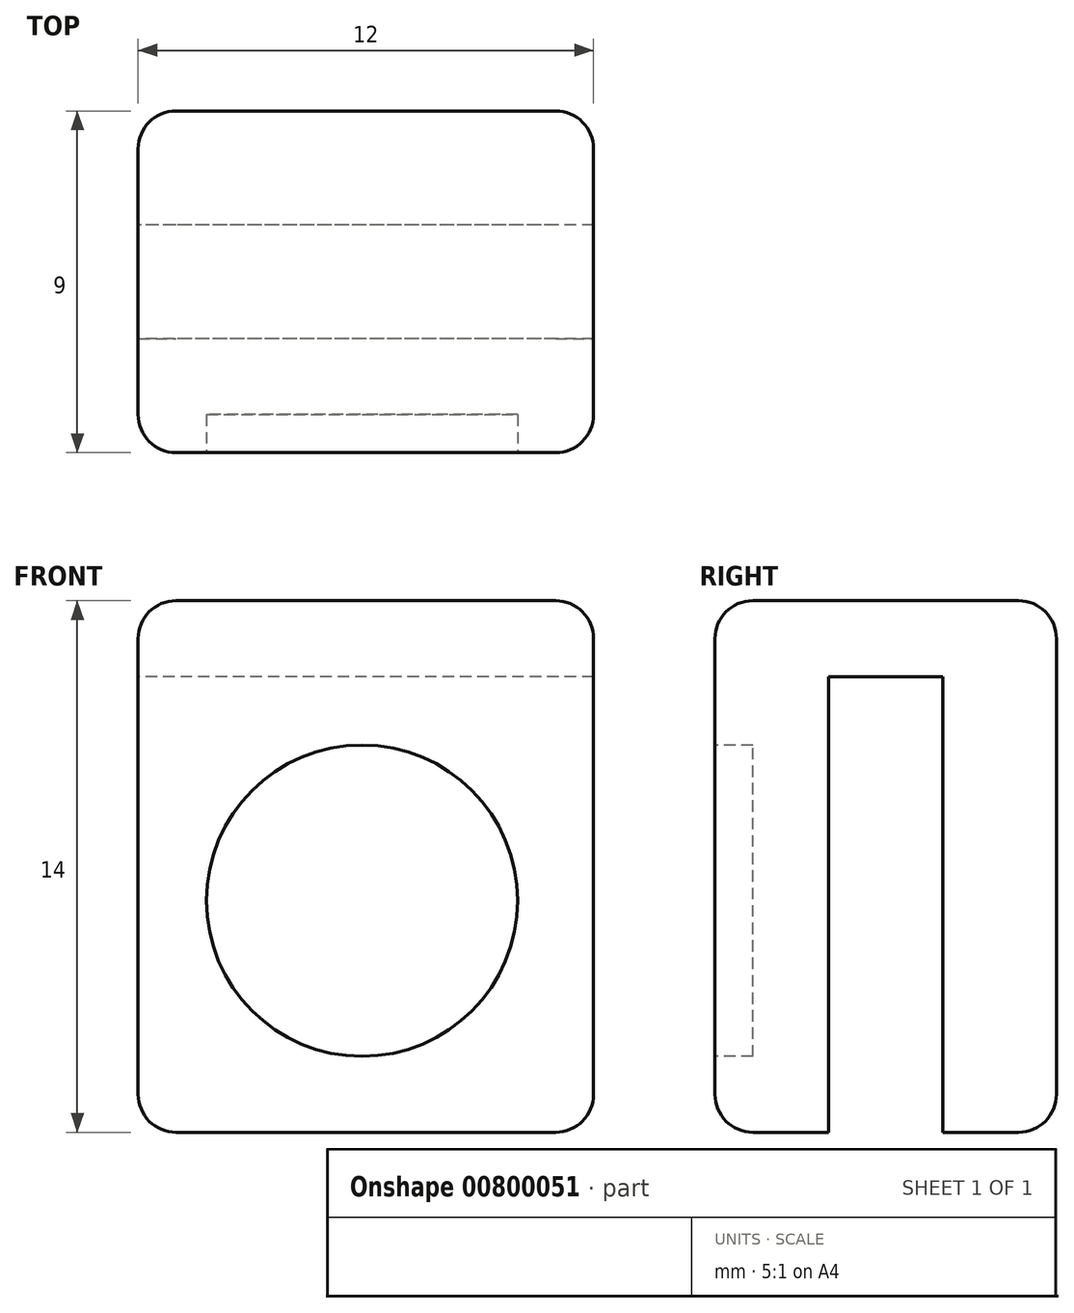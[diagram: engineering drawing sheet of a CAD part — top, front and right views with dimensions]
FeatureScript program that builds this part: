
annotation { "Feature Type Name" : "Feature", "Feature Type Description" : "" }
export const myFeature = defineFeature(function(context is Context, id is Id, definition is map)
    precondition{}
    {
        {
            var Q0;
            Q0=qCreatedBy(makeId("Front.planeOp"),FACE);
            var sketch = newSketch(context, id + "F0", { "sketchPlane" : qUnion([Q0])});
            skLineSegment(sketch, "E0", {"start": v(0, 0) * mm, "end": v(0, 14) * mm});
            skLineSegment(sketch, "E1", {"start": v(0, 14) * mm, "end": v(12, 14) * mm});
            skLineSegment(sketch, "E2", {"start": v(12, 14) * mm, "end": v(12, 0) * mm});
            skLineSegment(sketch, "E3", {"start": v(12, 0) * mm, "end": v(0, 0) * mm});
            skSolve(sketch);
        }
        {
            var Q0;
            Q0=makeQuery(id+"F0.imprint","IMPRINT",FACE,{"disambiguationData":[TD([[makeQuery(id+"F0.imprint","IMPRINT",EDGE,{"derivedFrom":sQuery(id+"F0.wireOp",EDGE,"E0")}),-1.0]])]});
            extrude(context, id + "F1", {"entities" : qUnion([Q0]), "depth" : 3 * mm, "offsetDistance" : 25 * mm});
        }
        {
            var Q0;
            Q0=makeQuery(id+"F1.opExtrude","CAP_FACE",FACE,{"disambiguationData":[OSD([sQuery(id+"F0.wireOp",EDGE,"E0"),sQuery(id+"F0.wireOp",EDGE,"E1"),sQuery(id+"F0.wireOp",EDGE,"E2"),sQuery(id+"F0.wireOp",EDGE,"E3")])],"isStart":false});
            var sketch = newSketch(context, id + "F2", { "sketchPlane" : qUnion([Q0])});
            skCircle(sketch, "E4", {"center": v(5.9, 6.1) * mm, "radius": 4.1 * mm});
            skSolve(sketch);
        }
        {
            var Q0;
            Q0=makeQuery(id+"F2.imprint","IMPRINT",FACE,{"disambiguationData":[TD([[makeQuery(id+"F2.imprint","IMPRINT",EDGE,{"derivedFrom":sQuery(id+"F2.wireOp",EDGE,"E4")}),1.0]])]});
            extrude(context, id + "F3", {"entities" : qUnion([Q0]), "operationType" : NewBodyOperationType.REMOVE, "oppositeDirection" : true, "depth" : 1 * mm, "offsetDistance" : 25 * mm});
        }
        {
            var Q0;
            Q0=makeQuery(id+"F1.opExtrude","CAP_FACE",FACE,{"disambiguationData":[OSD([sQuery(id+"F0.wireOp",EDGE,"E0"),sQuery(id+"F0.wireOp",EDGE,"E1"),sQuery(id+"F0.wireOp",EDGE,"E2"),sQuery(id+"F0.wireOp",EDGE,"E3")])],"isStart":true});
            var sketch = newSketch(context, id + "F4", { "sketchPlane" : qUnion([Q0])});
            skLineSegment(sketch, "E5.bottom", {"start": v(-12, 14) * mm, "end": v(0, 14) * mm});
            skLineSegment(sketch, "E5.top", {"start": v(-12, 12) * mm, "end": v(0, 12) * mm});
            skLineSegment(sketch, "E5.left", {"start": v(-12, 14) * mm, "end": v(-12, 12) * mm});
            skLineSegment(sketch, "E5.right", {"start": v(0, 14) * mm, "end": v(0, 12) * mm});
            skSolve(sketch);
        }
        {
            var Q0;
            Q0=makeQuery(id+"F4.imprint","IMPRINT",FACE,{"disambiguationData":[TD([[makeQuery(id+"F4.imprint","IMPRINT",EDGE,{"derivedFrom":sQuery(id+"F4.wireOp",EDGE,"E5.bottom")}),1.0]])]});
            extrude(context, id + "F5", {"entities" : qUnion([Q0]), "operationType" : NewBodyOperationType.ADD, "depth" : 3 * mm, "offsetDistance" : 25 * mm});
        }
        {
            var Q0;
            Q0=makeQuery(id+"F5.opExtrude","CAP_FACE",FACE,{"disambiguationData":[OSD([sQuery(id+"F4.wireOp",EDGE,"E5.bottom"),sQuery(id+"F4.wireOp",EDGE,"E5.top"),sQuery(id+"F4.wireOp",EDGE,"E5.left"),sQuery(id+"F4.wireOp",EDGE,"E5.right")])],"isStart":false});
            var sketch = newSketch(context, id + "F6", { "sketchPlane" : qUnion([Q0])});
            skLineSegment(sketch, "E6.bottom", {"start": v(-12, 14) * mm, "end": v(0, 14) * mm});
            skLineSegment(sketch, "E6.top", {"start": v(-12, 0) * mm, "end": v(0, 0) * mm});
            skLineSegment(sketch, "E6.left", {"start": v(-12, 14) * mm, "end": v(-12, 0) * mm});
            skLineSegment(sketch, "E6.right", {"start": v(0, 14) * mm, "end": v(0, 0) * mm});
            skSolve(sketch);
        }
        {
            var Q0;
            {var subQ0=sQuery(id+"F6.wireOp",EDGE,"E6.bottom");Q0=makeQuery(id+"F6.imprint","IMPRINT",FACE,{"disambiguationData":[TD([[makeQuery(id+"F6.imprint","IMPRINT",EDGE,{"derivedFrom":subQ0}),1.0]])]});}
            var Q1;
            {var subQ0=sQuery(id+"F6.wireOp",EDGE,"E6.top");Q1=makeQuery(id+"F6.imprint","IMPRINT",FACE,{"disambiguationData":[TD([[makeQuery(id+"F6.imprint","IMPRINT",EDGE,{"derivedFrom":subQ0}),1.0]])]});}
            extrude(context, id + "F7", {"entities" : qUnion([Q0, Q1]), "operationType" : NewBodyOperationType.ADD, "depth" : 3 * mm, "offsetDistance" : 25 * mm});
        }
        {
            var Q0;
            Q0=makeQuery(id+"F1.opExtrude","CAP_EDGE",EDGE,{"disambiguationData":[OSD([sQuery(id+"F0.wireOp",EDGE,"E2")])],"isStart":false});
            var Q1;
            Q1=makeQuery(id+"F1.opExtrude","CAP_EDGE",EDGE,{"disambiguationData":[OSD([sQuery(id+"F0.wireOp",EDGE,"E0")])],"isStart":false});
            var Q2;
            Q2=makeQuery(id+"F1.opExtrude","CAP_EDGE",EDGE,{"disambiguationData":[OSD([sQuery(id+"F0.wireOp",EDGE,"E1")])],"isStart":false});
            var Q3;
            Q3=makeQuery(id+"F1.opExtrude","CAP_EDGE",EDGE,{"disambiguationData":[OSD([sQuery(id+"F0.wireOp",EDGE,"E3")])],"isStart":false});
            var Q4;
            Q4=makeQuery(id+"F7.opExtrude","CAP_EDGE",EDGE,{"disambiguationData":[OSD([sQuery(id+"F6.wireOp",EDGE,"E6.bottom")])],"isStart":false});
            var Q5;
            Q5=makeQuery(id+"F7.opExtrude","CAP_EDGE",EDGE,{"disambiguationData":[OSD([sQuery(id+"F6.wireOp",EDGE,"E6.right")])],"isStart":false});
            var Q6;
            Q6=makeQuery(id+"F7.opExtrude","CAP_EDGE",EDGE,{"disambiguationData":[OSD([sQuery(id+"F6.wireOp",EDGE,"E6.left")])],"isStart":false});
            var Q7;
            Q7=makeQuery(id+"F7.opExtrude","CAP_EDGE",EDGE,{"disambiguationData":[OSD([sQuery(id+"F6.wireOp",EDGE,"E6.top")])],"isStart":false});
            var Q8;
            Q8=makeQuery(id+"F7.boolean.opBoolean","MERGE",EDGE,{"derivedFrom":[makeQuery(id+"F5.boolean.opBoolean","MERGE",EDGE,{"derivedFrom":[makeQuery(id+"F1.opExtrude","SWEPT_EDGE",EDGE,{"disambiguationData":[OSD([sQuery(id+"F0.wireOp",EDGE,"E0"),sQuery(id+"F0.wireOp",EDGE,"E1")])]}),makeQuery(id+"F5.opExtrude","SWEPT_EDGE",EDGE,{"disambiguationData":[OSD([sQuery(id+"F4.wireOp",EDGE,"E5.bottom"),sQuery(id+"F4.wireOp",EDGE,"E5.right")])]})]}),makeQuery(id+"F7.opExtrude","SWEPT_EDGE",EDGE,{"disambiguationData":[OSD([sQuery(id+"F6.wireOp",EDGE,"E6.bottom"),sQuery(id+"F6.wireOp",EDGE,"E6.right")])]})]});
            var Q9;
            Q9=makeQuery(id+"F7.boolean.opBoolean","MERGE",EDGE,{"derivedFrom":[makeQuery(id+"F5.boolean.opBoolean","MERGE",EDGE,{"derivedFrom":[makeQuery(id+"F1.opExtrude","SWEPT_EDGE",EDGE,{"disambiguationData":[OSD([sQuery(id+"F0.wireOp",EDGE,"E1"),sQuery(id+"F0.wireOp",EDGE,"E2")])]}),makeQuery(id+"F5.opExtrude","SWEPT_EDGE",EDGE,{"disambiguationData":[OSD([sQuery(id+"F4.wireOp",EDGE,"E5.bottom"),sQuery(id+"F4.wireOp",EDGE,"E5.left")])]})]}),makeQuery(id+"F7.opExtrude","SWEPT_EDGE",EDGE,{"disambiguationData":[OSD([sQuery(id+"F6.wireOp",EDGE,"E6.bottom"),sQuery(id+"F6.wireOp",EDGE,"E6.left")])]})]});
            var Q10;
            Q10=makeQuery(id+"F1.opExtrude","SWEPT_EDGE",EDGE,{"disambiguationData":[OSD([sQuery(id+"F0.wireOp",EDGE,"E2"),sQuery(id+"F0.wireOp",EDGE,"E3")])]});
            var Q11;
            Q11=makeQuery(id+"F7.opExtrude","SWEPT_EDGE",EDGE,{"disambiguationData":[OSD([sQuery(id+"F6.wireOp",EDGE,"E6.top"),sQuery(id+"F6.wireOp",EDGE,"E6.left")])]});
            var Q12;
            Q12=makeQuery(id+"F7.opExtrude","SWEPT_EDGE",EDGE,{"disambiguationData":[OSD([sQuery(id+"F6.wireOp",EDGE,"E6.top"),sQuery(id+"F6.wireOp",EDGE,"E6.right")])]});
            var Q13;
            Q13=makeQuery(id+"F1.opExtrude","SWEPT_EDGE",EDGE,{"disambiguationData":[OSD([sQuery(id+"F0.wireOp",EDGE,"E0"),sQuery(id+"F0.wireOp",EDGE,"E3")])]});
            fillet(context, id + "F8", {"entities" : qUnion([Q0, Q1, Q2, Q3, Q4, Q5, Q6, Q7, Q8, Q9, Q10, Q11, Q12, Q13]), "radius" : 1 * mm, "tangentPropagation" : true, "allowEdgeOverflow" : false});
        }
    });
